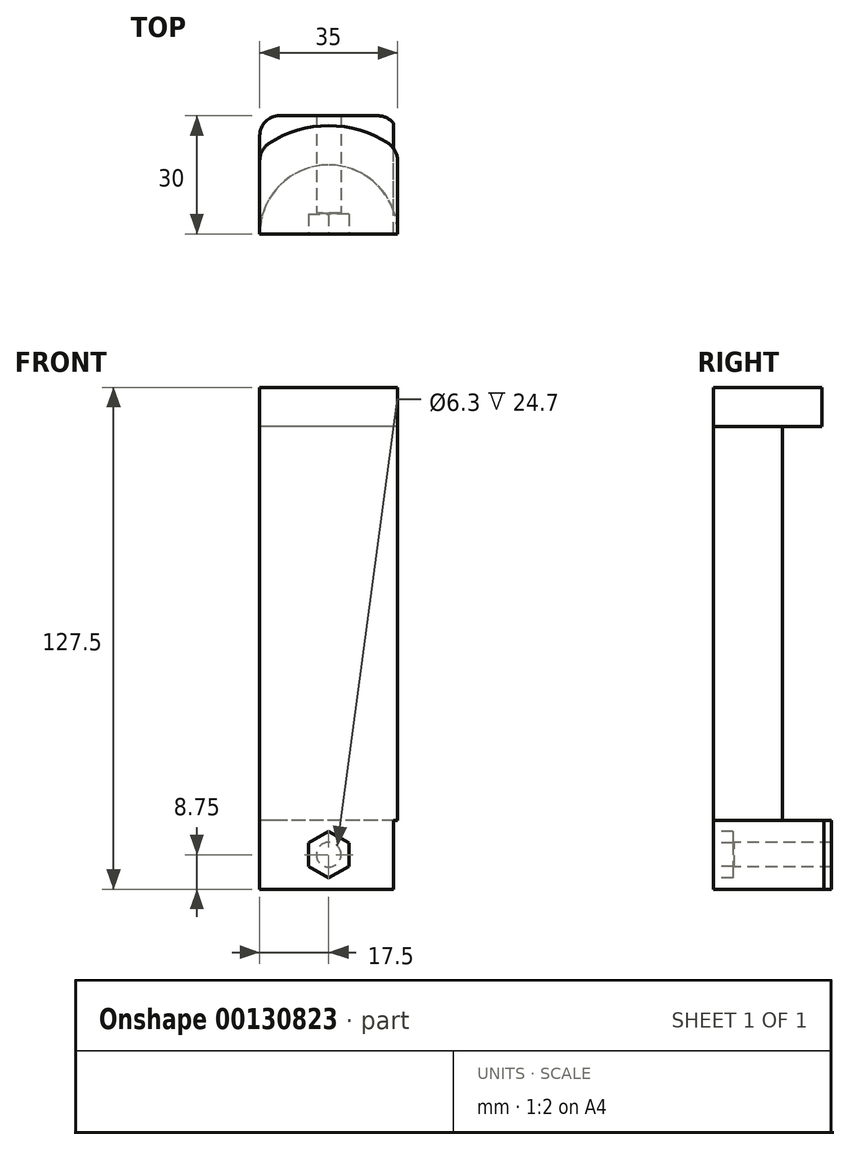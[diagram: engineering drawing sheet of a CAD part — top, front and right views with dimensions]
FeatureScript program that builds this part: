
annotation { "Feature Type Name" : "Feature", "Feature Type Description" : "" }
export const myFeature = defineFeature(function(context is Context, id is Id, definition is map)
    precondition{}
    {
        {
            assignVariable(context, id + "F0", {"name" : "x", "anyValue" : 35});
        }
        {
            assignVariable(context, id + "F1", {"name" : "NussTiefe", "anyValue" : 5});
        }
        {
            var Q0;
            Q0=qCreatedBy(makeId("Top.planeOp"),FACE);
            var sketch = newSketch(context, id + "F2", { "sketchPlane" : qUnion([Q0])});
            skLineSegment(sketch, "E0.bottom", {"start": v(17.5, -15) * mm, "end": v(-17.5, -15) * mm});
            skLineSegment(sketch, "E0.top", {"start": v(17.5, 15) * mm, "end": v(-17.5, 15) * mm});
            skLineSegment(sketch, "E0.left", {"start": v(17.5, -15) * mm, "end": v(17.5, 15) * mm});
            skLineSegment(sketch, "E0.right", {"start": v(-17.5, -15) * mm, "end": v(-17.5, 15) * mm});
            skPoint(sketch, "E0.middle", {"position": v(0, 0) * mm});
            skArc(sketch, "E1", {"start": v(17.5, -15) * mm, "mid": v(0, 2.5) * mm, "end": v(-17.5, -15) * mm});
            skSolve(sketch);
        }
        {
            var Q0;
            Q0=qSketchRegion(id+"F2",true);
            extrude(context, id + "F3", {"entities" : qUnion([Q0]), "endBound" : BoundingType.SYMMETRIC, "depth" : (getVariable(context, 'x') / 2) * mm});
        }
        {
            var Q0;
            Q0=makeQuery(id+"F3.opExtrude","CAP_FACE",FACE,{"disambiguationData":[OSD([sQuery(id+"F2.wireOp",EDGE,"E0.bottom"),sQuery(id+"F2.wireOp",EDGE,"E0.top"),sQuery(id+"F2.wireOp",EDGE,"E0.left"),sQuery(id+"F2.wireOp",EDGE,"E0.right")])],"isStart":false});
            var sketch = newSketch(context, id + "F4", { "sketchPlane" : qUnion([Q0])});
            skArc(sketch, "E2.0", {"start": v(17.5, -15) * mm, "mid": v(0, 2.5) * mm, "end": v(-17.5, -15) * mm});
            skSolve(sketch);
        }
        {
            var Q0;
            Q0=makeQuery(id+"F3.opExtrude","SWEPT_FACE",FACE,{"disambiguationData":[OSD([sQuery(id+"F2.wireOp",EDGE,"E0.bottom")])]});
            var sketch = newSketch(context, id + "F5", { "sketchPlane" : qUnion([Q0])});
            skCircle(sketch, "E3", {"center": v(0, 0) * mm, "radius": 3.15 * mm});
            skCircle(sketch, "E4.cCircle", {"center": v(0, 0) * mm, "radius": 5.15 * mm, "construction": true});
            skLineSegment(sketch, "E4.0", {"start": v(5.15, -2.97) * mm, "end": v(0, -5.95) * mm});
            skLineSegment(sketch, "E4.1", {"start": v(0, -5.95) * mm, "end": v(-5.15, -2.97) * mm});
            skLineSegment(sketch, "E4.2", {"start": v(-5.15, -2.97) * mm, "end": v(-5.15, 2.97) * mm});
            skLineSegment(sketch, "E4.3", {"start": v(-5.15, 2.97) * mm, "end": v(0, 5.95) * mm});
            skLineSegment(sketch, "E4.4", {"start": v(0, 5.95) * mm, "end": v(5.15, 2.97) * mm});
            skLineSegment(sketch, "E4.5", {"start": v(5.15, 2.97) * mm, "end": v(5.15, -2.97) * mm});
            skPoint(sketch, "E4.0.midPoint", {"position": v(2.58, -4.46) * mm});
            skSolve(sketch);
        }
        {
            var Q0;
            Q0=makeQuery(id+"F5.imprint","IMPRINT",FACE,{"disambiguationData":[TD([[makeQuery(id+"F5.imprint","IMPRINT",EDGE,{"derivedFrom":sQuery(id+"F5.wireOp",EDGE,"E3")}),1.0]])]});
            extrude(context, id + "F6", {"entities" : qUnion([Q0]), "operationType" : NewBodyOperationType.REMOVE, "endBound" : BoundingType.UP_TO_NEXT, "oppositeDirection" : true, "depth" : 25 * mm});
        }
        {
            var Q0;
            Q0=makeQuery(id+"F5.imprint","IMPRINT",FACE,{"disambiguationData":[TD([[makeQuery(id+"F5.imprint","IMPRINT",EDGE,{"derivedFrom":sQuery(id+"F5.wireOp",EDGE,"E3")}),-1.0]])]});
            extrude(context, id + "F7", {"entities" : qUnion([Q0]), "operationType" : NewBodyOperationType.REMOVE, "oppositeDirection" : true, "depth" : (getVariable(context, 'NussTiefe')) * mm});
        }
        {
            var Q0;
            Q0=makeQuery(id+"F3.opExtrude","SWEPT_FACE",FACE,{"disambiguationData":[OSD([sQuery(id+"F2.wireOp",EDGE,"E0.left")])]});
            var sketch = newSketch(context, id + "F8", { "sketchPlane" : qUnion([Q0])});
            skText(sketch, "E5", { "text": "R", "fontName": "OpenSans-Bold.ttf"});
            skPoint(sketch, "E6", {"position": v(1.38, 0) * mm});
            skLineSegment(sketch, "E7", {"start": v(-9.1, -4) * mm, "end": v(-9.1, 4) * mm});
            const initialGuessF8  = {"E5": [-0.0091, 0.004, 0, -1, 0.00794]};
            skSetInitialGuess(sketch, initialGuessF8);
            skSolve(sketch);
        }
        {
            var Q0;
            Q0=makeQuery(id+"F4.imprint","IMPRINT",FACE,{"disambiguationData":[TD([[makeQuery(id+"F4.imprint","IMPRINT",EDGE,{"derivedFrom":sQuery(id+"F4.wireOp",EDGE,"E2.0")}),1.0]])]});
            extrude(context, id + "F9", {"entities" : qUnion([Q0]), "operationType" : NewBodyOperationType.ADD, "depth" : 100 * mm});
        }
        {
            var Q0;
            Q0=makeQuery(id+"F9.opExtrude","CAP_FACE",FACE,{"disambiguationData":[OSD([sQuery(id+"F2.wireOp",EDGE,"E0.bottom"),sQuery(id+"F4.wireOp",EDGE,"E2.0")])],"isStart":false});
            var sketch = newSketch(context, id + "F10", { "sketchPlane" : qUnion([Q0])});
            skArc(sketch, "E8", {"start": v(17.5, 6.21) * mm, "mid": v(0, 12.5) * mm, "end": v(-17.5, 6.21) * mm});
            skLineSegment(sketch, "E9", {"start": v(-17.5, -15) * mm, "end": v(-17.5, 6.21) * mm});
            skLineSegment(sketch, "E10", {"start": v(17.5, -15) * mm, "end": v(17.5, 6.21) * mm});
            skSolve(sketch);
        }
        {
            var Q0;
            Q0=makeQuery(id+"F10.imprint","IMPRINT",FACE,{"disambiguationData":[TD([[makeQuery(id+"F10.imprint","IMPRINT",EDGE,{"derivedFrom":sQuery(id+"F10.wireOp",EDGE,"E8")}),1.0]])]});
            var Q1;
            Q1=makeQuery(id+"F10.imprint","IMPRINT",FACE,{"disambiguationData":[TD([[makeQuery(id+"F10.imprint","IMPRINT",EDGE,{"derivedFrom":makeQuery(id+"F9.opExtrude","CAP_EDGE",EDGE,{"disambiguationData":[OSD([sQuery(id+"F4.wireOp",EDGE,"E2.0")])],"isStart":false})}),1.0]])]});
            extrude(context, id + "F11", {"entities" : qUnion([Q0, Q1]), "operationType" : NewBodyOperationType.ADD, "depth" : 10 * mm});
        }
        {
            var Q0;
            Q0=makeQuery(id+"F11.opExtrude","SWEPT_EDGE",EDGE,{"disambiguationData":[OSD([sQuery(id+"F10.wireOp",EDGE,"E8"),sQuery(id+"F10.wireOp",EDGE,"E9")])]});
            var Q1;
            Q1=makeQuery(id+"F3.opExtrude","SWEPT_EDGE",EDGE,{"disambiguationData":[OSD([sQuery(id+"F2.wireOp",EDGE,"E0.top"),sQuery(id+"F2.wireOp",EDGE,"E0.right")])]});
            var Q2;
            Q2=makeQuery(id+"F3.opExtrude","SWEPT_EDGE",EDGE,{"disambiguationData":[OSD([sQuery(id+"F2.wireOp",EDGE,"E0.top"),sQuery(id+"F2.wireOp",EDGE,"E0.left")])]});
            var Q3;
            Q3=makeQuery(id+"F11.opExtrude","SWEPT_EDGE",EDGE,{"disambiguationData":[OSD([sQuery(id+"F10.wireOp",EDGE,"E8"),sQuery(id+"F10.wireOp",EDGE,"E10")])]});
            fillet(context, id + "F12", {"entities" : qUnion([Q0, Q1, Q2, Q3]), "radius" : 5 * mm, "tangentPropagation" : true, "allowEdgeOverflow" : false});
        }
        {
            var Q0;
            Q0=makeQuery(id+"F8.imprint","IMPRINT",FACE,{"disambiguationData":[TD([[makeQuery(id+"F8.imprint","IMPRINT",EDGE,{"derivedFrom":sQuery(id+"F8.wireOp",EDGE,"E5.sketch_text.stroke-0")}),-1.0]])]});
            var Q1;
            {var subQ0=sQuery(id+"F8.wireOp",EDGE,"E5.sketch_text.stroke-7");Q1=makeQuery(id+"F8.imprint","IMPRINT",FACE,{"disambiguationData":[TD([[makeQuery(id+"F8.imprint","IMPRINT",EDGE,{"derivedFrom":subQ0}),1.0]])]});}
            var Q2;
            Q2=makeQuery(id+"F8.imprint","IMPRINT",FACE,{"disambiguationData":[TD([[makeQuery(id+"F8.imprint","IMPRINT",EDGE,{"derivedFrom":sQuery(id+"F8.wireOp",EDGE,"E5.sketch_text.stroke-0")}),1.0]])]});
            extrude(context, id + "F13", {"entities" : qUnion([Q0, Q1, Q2]), "operationType" : NewBodyOperationType.REMOVE, "oppositeDirection" : true, "depth" : 1 * mm});
        }
        {
            var Q0;
            Q0=makeQuery(id+"F7.boolean.opBoolean","COPY",FACE,{"derivedFrom":makeQuery(id+"F7.opExtrude","CAP_FACE",FACE,{"disambiguationData":[OSD([sQuery(id+"F5.wireOp",EDGE,"E3"),sQuery(id+"F5.wireOp",EDGE,"E4.0"),sQuery(id+"F5.wireOp",EDGE,"E4.1"),sQuery(id+"F5.wireOp",EDGE,"E4.2"),sQuery(id+"F5.wireOp",EDGE,"E4.3"),sQuery(id+"F5.wireOp",EDGE,"E4.4"),sQuery(id+"F5.wireOp",EDGE,"E4.5")])],"isStart":false})});
            var sketch = newSketch(context, id + "F14", { "sketchPlane" : qUnion([Q0])});
            skCircle(sketch, "E11", {"center": v(0, 0) * mm, "radius": 3.95 * mm});
            skSolve(sketch);
        }
        {
            var Q0;
            Q0 = qSketchRegion(id + "F14", true);
            extrude(context, id + "F15", {"entities" : qUnion([Q0]), "operationType" : NewBodyOperationType.ADD, "oppositeDirection" : true, "depth" : 0.3 * mm});
        }
    });
